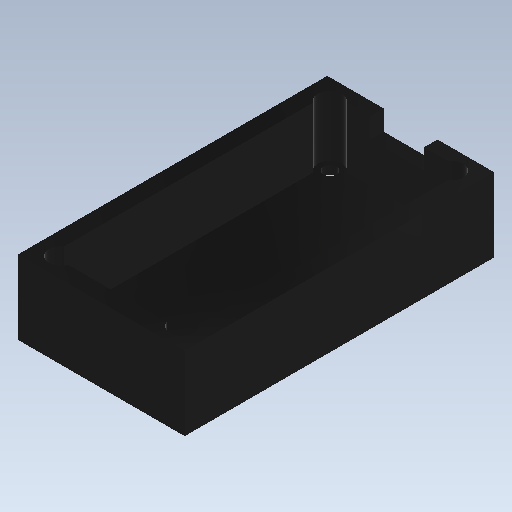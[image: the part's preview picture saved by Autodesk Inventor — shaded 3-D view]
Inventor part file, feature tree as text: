
AUTODESK INVENTOR PART (.ipt)
format: ipt  version: 2020 (Build 240168000, 168)  size: 150,016 bytes
history: native  units: mm
features: sketch x5, extrude x4, projected_geometry x2, other x1, hole x1
ambient origin geometry x8: Origin, YZ Plane, XZ Plane, XY Plane, X Axis, Y Axis, Z Axis, Center Point
bodies: Body1 (feature_tree)
feature tree (13):
  other  "Твердое тело1"
  extrude  "Выдавливание1"  Depth=12.4mm
  extrude  "Выдавливание2"  Depth=23.0mm
  hole  "Отверстие1"  [1 undecoded]
  extrude  "Выдавливание3"  Depth=1.0mm
  extrude  "Выдавливание4"  Depth=1.2mm
  sketch  "Эскиз1"
  sketch  "Эскиз2"
  projected_geometry  "Спроецированная петля1"
  sketch  "Эскиз3"
  sketch  "Эскиз4"
  sketch  "Эскиз5"
  projected_geometry  "Спроецированная петля2"
note: 1 required parameter value undecoded (feature->parameter linkage not recoverable at this tier; creation-order binding heuristic only, values carry confidence <= 0.55)
